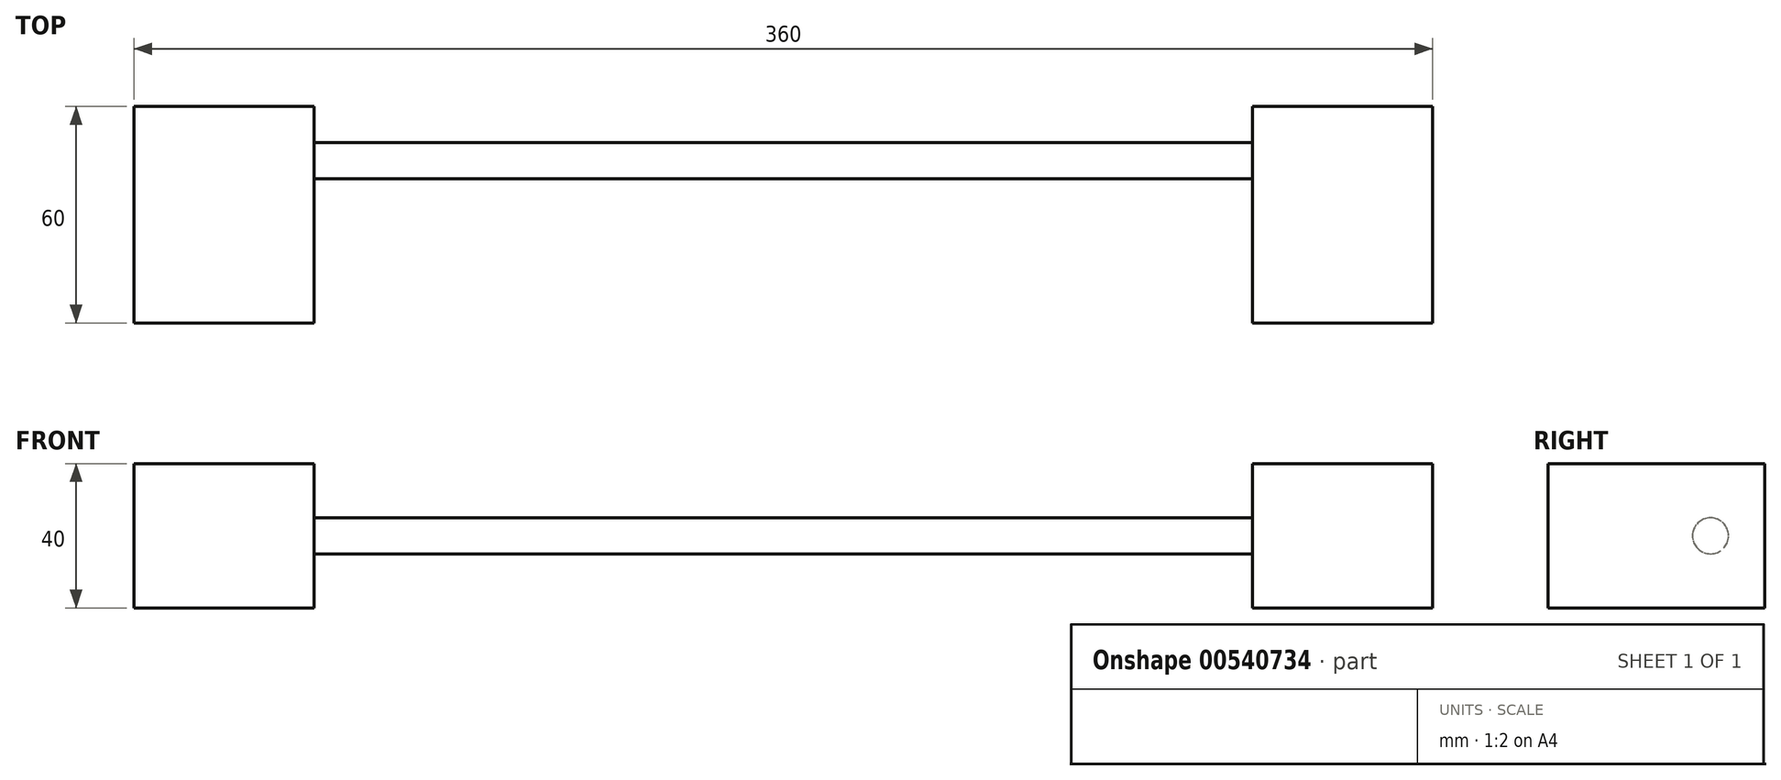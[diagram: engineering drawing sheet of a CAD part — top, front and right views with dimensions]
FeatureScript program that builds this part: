
annotation { "Feature Type Name" : "Feature", "Feature Type Description" : "" }
export const myFeature = defineFeature(function(context is Context, id is Id, definition is map)
    precondition{}
    {
        {
            var Q0;
            Q0=qCreatedBy(makeId("Top.planeOp"),FACE);
            var sketch = newSketch(context, id + "F0", { "sketchPlane" : qUnion([Q0])});
            skLineSegment(sketch, "E0", {"start": v(-175.64, -60) * mm, "end": v(229.54, -60) * mm, "construction": true});
            skLineSegment(sketch, "E1.bottom", {"start": v(-150, -60) * mm, "end": v(-100, -60) * mm});
            skLineSegment(sketch, "E1.top", {"start": v(-150, 0) * mm, "end": v(-100, 0) * mm});
            skLineSegment(sketch, "E1.left", {"start": v(-150, -60) * mm, "end": v(-150, 0) * mm});
            skLineSegment(sketch, "E1.right", {"start": v(-100, -60) * mm, "end": v(-100, 0) * mm});
            skLineSegment(sketch, "E2", {"start": v(-100, 0) * mm, "end": v(208.6, 0) * mm, "construction": true});
            skLineSegment(sketch, "E3.bottom", {"start": v(210, 0) * mm, "end": v(160, 0) * mm});
            skLineSegment(sketch, "E3.top", {"start": v(210, -60) * mm, "end": v(160, -60) * mm});
            skLineSegment(sketch, "E3.left", {"start": v(210, 0) * mm, "end": v(210, -60) * mm});
            skLineSegment(sketch, "E3.right", {"start": v(160, 0) * mm, "end": v(160, -60) * mm});
            skSolve(sketch);
        }
        {
            var Q0;
            Q0=makeQuery(id+"F0.imprint","IMPRINT",FACE,{"disambiguationData":[TD([[makeQuery(id+"F0.imprint","IMPRINT",EDGE,{"derivedFrom":sQuery(id+"F0.wireOp",EDGE,"E1.bottom")}),1.0]])]});
            var Q1;
            Q1=makeQuery(id+"F0.imprint","IMPRINT",FACE,{"disambiguationData":[TD([[makeQuery(id+"F0.imprint","IMPRINT",EDGE,{"derivedFrom":sQuery(id+"F0.wireOp",EDGE,"E3.bottom")}),1.0]])]});
            extrude(context, id + "F1", {"entities" : qUnion([Q0, Q1]), "depth" : 40 * mm, "offsetDistance" : 25 * mm});
        }
        {
            var Q0;
            Q0=makeQuery(id+"F1.opExtrude","SWEPT_FACE",FACE,{"disambiguationData":[OSD([sQuery(id+"F0.wireOp",EDGE,"E3.left")])]});
            var sketch = newSketch(context, id + "F2", { "sketchPlane" : qUnion([Q0])});
            skCircle(sketch, "E4", {"center": v(-15, 20) * mm, "radius": 5 * mm});
            skPoint(sketch, "E4.centerSnap0", {"position": v(-30, 40) * mm});
            skSolve(sketch);
        }
        {
            var Q0;
            Q0=qSketchRegion(id+"F2",true);
            var Q1;
            Q1=makeQuery(id+"F1.opExtrude","SWEPT_FACE",FACE,{"disambiguationData":[OSD([sQuery(id+"F0.wireOp",EDGE,"E1.right")])]});
            var Q2;
            Q2=makeQuery(id+"F1.opExtrude","SWEPT_FACE",FACE,{"disambiguationData":[OSD([sQuery(id+"F0.wireOp",EDGE,"E3.right")])]});
            extrude(context, id + "F3", {"entities" : qUnion([Q0]), "endBound" : BoundingType.UP_TO_SURFACE, "oppositeDirection" : true, "depth" : 321.9 * mm, "endBoundEntityFace" : qUnion([Q1]), "offsetDistance" : 25 * mm, "hasSecondDirection" : true, "secondDirectionBound" : SecondDirectionBoundingType.UP_TO_SURFACE, "secondDirectionOppositeDirection" : true, "secondDirectionDepth" : 25 * mm, "secondDirectionBoundEntityFace" : qUnion([Q2])});
        }
    });
